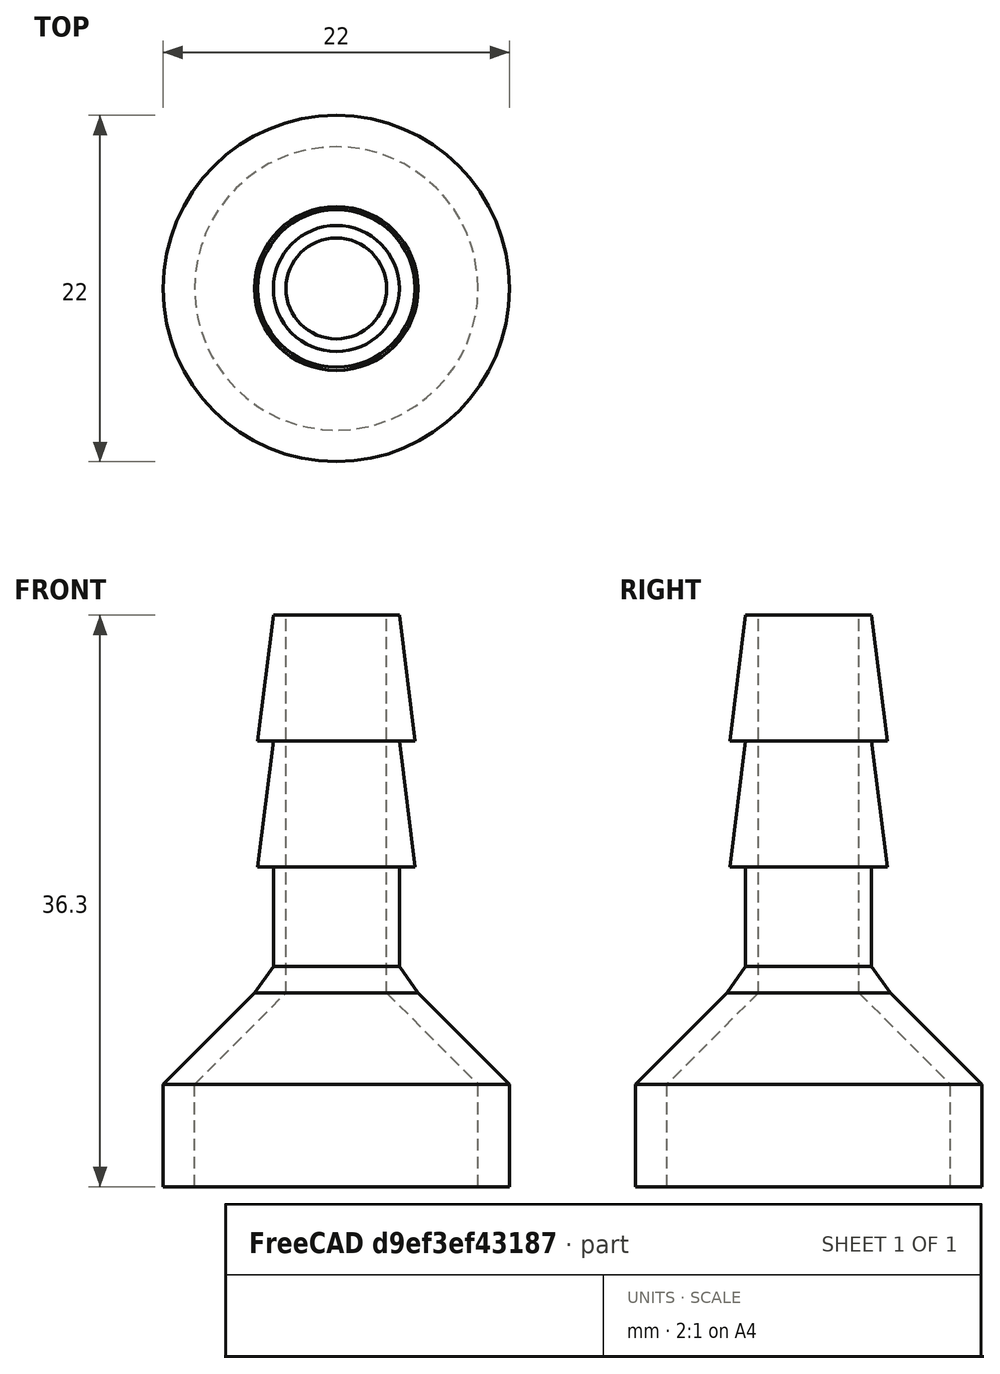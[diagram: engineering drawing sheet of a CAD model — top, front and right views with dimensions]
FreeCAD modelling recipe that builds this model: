
FCSTD DOCUMENT  (FreeCAD 0.18R16110 (Git))
Label: pumpnosle
License: All rights reserved
LicenseURL: http://en.wikipedia.org/wiki/All_rights_reserved
objects: Sketcher::SketchObject×1, PartDesign::Revolution×1, PartDesign::Body×1
note: 4 computed .brp shape members not serialized (recipe doc carries the construction recipe); baked Part::Feature solids carry a one-line shape summary decoded from their .brp

FEATURE [Sketcher::SketchObject] Sketch
  MapMode = 5
  Placement = pos=(0,0,0) rot=(1,0,0;1.5708rad)
  Support = -> [XZ_Plane]
  sketch-geometry (18):
    g0: LineSegment StartX=-9 StartY=0 StartZ=0 EndX=-11 EndY=0 EndZ=0
    g1: LineSegment StartX=-11 StartY=0 StartZ=0 EndX=-11 EndY=6.5 EndZ=0
    g2: LineSegment StartX=-9 StartY=0 StartZ=0 EndX=-9 EndY=6.5 EndZ=0
    g3: LineSegment [constr] StartX=0 StartY=0 StartZ=0 EndX=-3.2 EndY=0 EndZ=0
    g4: LineSegment [constr] StartX=-3.2 StartY=0 StartZ=0 EndX=-3.2 EndY=12.3 EndZ=0
    g5: LineSegment StartX=-9 StartY=6.5 StartZ=0 EndX=-3.2 EndY=12.3 EndZ=0
    g6: LineSegment StartX=-3.2 StartY=12.3 StartZ=0 EndX=-3.2 EndY=36.3 EndZ=0
    g7: LineSegment StartX=-3.2 StartY=36.3 StartZ=0 EndX=-4 EndY=36.3 EndZ=0
    g8: LineSegment [constr] StartX=-4 StartY=36.3 StartZ=0 EndX=-4 EndY=28.3 EndZ=0
    g9: LineSegment StartX=-4 StartY=28.3 StartZ=0 EndX=-5 EndY=28.3 EndZ=0
    g10: LineSegment StartX=-4 StartY=36.3 StartZ=0 EndX=-5 EndY=28.3 EndZ=0
    g11: LineSegment [constr] StartX=-4 StartY=28.3 StartZ=0 EndX=-4 EndY=20.3 EndZ=0
    g12: LineSegment StartX=-4 StartY=20.3 StartZ=0 EndX=-5 EndY=20.3 EndZ=0
    g13: LineSegment StartX=-4 StartY=28.3 StartZ=0 EndX=-5 EndY=20.3 EndZ=0
    g14: LineSegment [constr] StartX=-3.2 StartY=12.3 StartZ=0 EndX=-5.2 EndY=12.3 EndZ=0
    g15: LineSegment StartX=-11 StartY=6.5 StartZ=0 EndX=-5.2 EndY=12.3 EndZ=0
    g16: LineSegment StartX=-4 StartY=20.3 StartZ=0 EndX=-4 EndY=14 EndZ=0
    g17: LineSegment StartX=-5.2 StartY=12.3 StartZ=0 EndX=-4 EndY=14 EndZ=0
  constraints (50):
    c: Horizontal(g0)
    c: DistanceX(g0) = -11
    c: Coincident(g1,g0)
    c: Vertical(g1)
    c: DistanceY(g1) = 6.5
    c: Coincident(g2,g0)
    c: Vertical(g2)
    c: DistanceY(g2) = 6.5
    c: DistanceX(g0) = -9
    c: DistanceY(g0) = 0
    c: Coincident(g3,g-1)
    c: PointOnObject(g3,g-1)
    c: DistanceX(g3) = -3.2
    c: Coincident(g4,g3)
    c: Vertical(g4)
    c: DistanceY(g4) = 12.3
    c: Coincident(g5,g2)
    c: Coincident(g5,g4)
    c: Coincident(g6,g5)
    c: Vertical(g6)
    c: DistanceY(g6) = 36.3
    c: Coincident(g7,g6)
    c: Horizontal(g7)
    c: DistanceX(g7) = -4
    c: Coincident(g8,g7)
    c: Vertical(g8)
    c: DistanceY(g8) = 28.3
    c: Coincident(g9,g8)
    c: Horizontal(g9)
    c: DistanceX(g9) = -5
    c: Coincident(g10,g7)
    c: Coincident(g10,g9)
    c: Coincident(g11,g9)
    c: Vertical(g11)
    c: DistanceY(g11) = 20.3
    c: Coincident(g12,g11)
    c: Horizontal(g12)
    c: DistanceX(g12) = -5
    c: Coincident(g13,g9)
    c: Coincident(g13,g12)
    c: Coincident(g14,g5)
    c: Horizontal(g14)
    c: DistanceX(g14) = -5.2
    c: Coincident(g15,g1)
    c: Coincident(g15,g14)
    c: Coincident(g16,g12)
    c: Vertical(g16)
    c: DistanceY(g16) = 14
    c: Coincident(g17,g15)
    c: Coincident(g17,g16)
FEATURE [PartDesign::Revolution] Revolution
  Angle = 360
  Axis = (0,2e-16,1)
  Base = (0,0,0)
  Placement = pos=(0,0,0) rot=(1,0,0;1.5708rad)
  Profile = -> Sketch
  ReferenceAxis = -> Sketch [V_Axis]
FEATURE [PartDesign::Body] Body
  Group = -> [Sketch,Revolution]
  Origin = -> Origin
  Tip = -> Revolution
